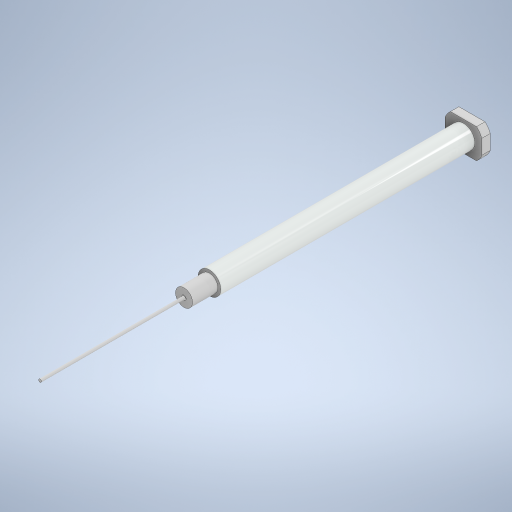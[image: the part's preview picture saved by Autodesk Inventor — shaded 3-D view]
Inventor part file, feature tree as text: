
AUTODESK INVENTOR PART (.ipt)
format: ipt  version: 2023.2 (Build 272271000, 271)  size: 282,624 bytes
history: native  units: mm
features: extrude x6, sketch x5
ambient origin geometry x8: Origin, YZ Plane, XZ Plane, XY Plane, X Axis, Y Axis, Z Axis, Center Point
bodies: Solid1 (feature_tree)
feature tree (11):
  extrude  "Extrusion1"  Depth=99.0mm TaperAngle=0.0deg
  extrude  "Extrusion2"  Depth=9.0mm TaperAngle=0.0deg
  extrude  "Extrusion3"  TaperAngle=0.0deg  [1 undecoded]
  extrude  "Extrusion4"  Depth=51.0mm TaperAngle=0.0deg
  sketch  "Sketch6"  dims[d12=13.0mm d13=10.5mm d14=3.0mm d15=0.0mm d16=14.0mm d17=3.0mm d18=0.0mm]
  extrude  "Extrusion5"  Depth=10.5mm
  extrude  "Extrusion6"  Depth=3.0mm TaperAngle=0.0deg
  sketch  "Sketch1"  dims[d0=8.0mm d1=99.0mm d2=0.0mm]
  sketch  "Sketch2"  dims[d3=6.0mm d4=9.0mm d5=0.0mm]
  sketch  "Sketch3"  dims[d6=1.5mm d7=0.0mm d8=0.0mm]
  sketch  "Sketch5"  dims[d9=1.0mm d10=51.0mm d11=0.0mm]
note: 1 required parameter value undecoded (feature->parameter linkage not recoverable at this tier; creation-order binding heuristic only, values carry confidence <= 0.55)
